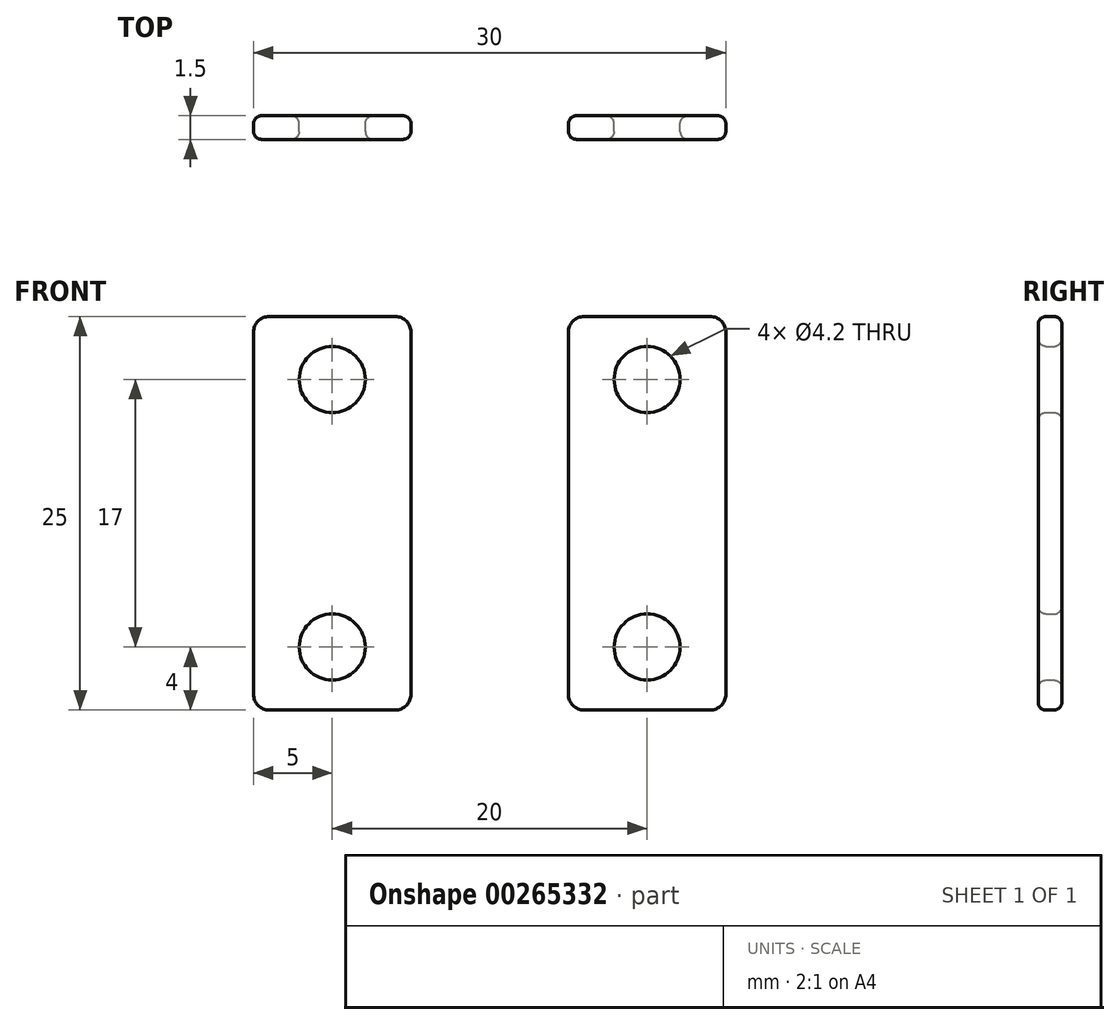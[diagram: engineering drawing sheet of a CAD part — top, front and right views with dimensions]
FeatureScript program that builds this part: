
annotation { "Feature Type Name" : "Feature", "Feature Type Description" : "" }
export const myFeature = defineFeature(function(context is Context, id is Id, definition is map)
    precondition{}
    {
        {
            var Q0;
            Q0=qCreatedBy(makeId("Front.planeOp"),FACE);
            var sketch = newSketch(context, id + "F0", { "sketchPlane" : qUnion([Q0])});
            skLineSegment(sketch, "E0.bottom", {"start": v(6, 12.5) * mm, "end": v(14, 12.5) * mm});
            skLineSegment(sketch, "E0.top", {"start": v(6, -12.5) * mm, "end": v(14, -12.5) * mm});
            skLineSegment(sketch, "E0.left", {"start": v(5, 11.5) * mm, "end": v(5, -11.5) * mm});
            skLineSegment(sketch, "E0.right", {"start": v(15, 11.5) * mm, "end": v(15, -11.5) * mm});
            skCircle(sketch, "E1", {"center": v(10, 8.5) * mm, "radius": 2.1 * mm});
            skCircle(sketch, "E2", {"center": v(10, -8.5) * mm, "radius": 2.1 * mm});
            skPoint(sketch, "E3.visualSharp", {"position": v(5, 12.5) * mm});
            skArc(sketch, "E3.filletArc", {"start": v(6, 12.5) * mm, "mid": v(5.3, 12.2) * mm, "end": v(5, 11.5) * mm});
            skPoint(sketch, "E4.visualSharp", {"position": v(15, 12.5) * mm});
            skArc(sketch, "E4.filletArc", {"start": v(15, 11.5) * mm, "mid": v(14.7, 12.2) * mm, "end": v(14, 12.5) * mm});
            skPoint(sketch, "E5.visualSharp", {"position": v(15, -12.5) * mm});
            skArc(sketch, "E5.filletArc", {"start": v(14, -12.5) * mm, "mid": v(14.7, -12.2) * mm, "end": v(15, -11.5) * mm});
            skPoint(sketch, "E6.visualSharp", {"position": v(5, -12.5) * mm});
            skArc(sketch, "E6.filletArc", {"start": v(5, -11.5) * mm, "mid": v(5.3, -12.2) * mm, "end": v(6, -12.5) * mm});
            skLineSegment(sketch, "E7.MirrorCS", {"start": v(-6, 12.5) * mm, "end": v(-14, 12.5) * mm});
            skLineSegment(sketch, "E8.MirrorCS", {"start": v(-15, 11.5) * mm, "end": v(-15, -11.5) * mm});
            skLineSegment(sketch, "E9.MirrorCS", {"start": v(-6, -12.5) * mm, "end": v(-14, -12.5) * mm});
            skLineSegment(sketch, "E10.MirrorCS", {"start": v(-5, 11.5) * mm, "end": v(-5, -11.5) * mm});
            skCircle(sketch, "E11.MirrorC", {"center": v(-10, 8.5) * mm, "radius": 2.1 * mm});
            skCircle(sketch, "E12.MirrorC", {"center": v(-10, -8.5) * mm, "radius": 2.1 * mm});
            skArc(sketch, "E13.MirrorCS", {"start": v(-5, -11.5) * mm, "mid": v(-5.3, -12.2) * mm, "end": v(-6, -12.5) * mm});
            skArc(sketch, "E14.MirrorCS", {"start": v(-14, -12.5) * mm, "mid": v(-14.7, -12.2) * mm, "end": v(-15, -11.5) * mm});
            skArc(sketch, "E15.MirrorCS", {"start": v(-15, 11.5) * mm, "mid": v(-14.7, 12.2) * mm, "end": v(-14, 12.5) * mm});
            skArc(sketch, "E16.MirrorCS", {"start": v(-6, 12.5) * mm, "mid": v(-5.3, 12.2) * mm, "end": v(-5, 11.5) * mm});
            skSolve(sketch);
        }
        {
            var Q0;
            Q0 = qSketchRegion(id + "F0", true);
            extrude(context, id + "F1", {"entities" : qUnion([Q0]), "depth" : 1.5 * mm});
        }
        {
            var Q0;
            Q0=makeQuery(id+"F1.opExtrude","CAP_EDGE",EDGE,{"disambiguationData":[OSD([sQuery(id+"F0.wireOp",EDGE,"E8.MirrorCS")])],"isStart":false});
            var Q1;
            Q1=makeQuery(id+"F1.opExtrude","CAP_EDGE",EDGE,{"disambiguationData":[OSD([sQuery(id+"F0.wireOp",EDGE,"E0.left")])],"isStart":false});
            var Q2;
            Q2=makeQuery(id+"F1.opExtrude","CAP_EDGE",EDGE,{"disambiguationData":[OSD([sQuery(id+"F0.wireOp",EDGE,"E11.MirrorC")])],"isStart":false});
            var Q3;
            Q3=makeQuery(id+"F1.opExtrude","CAP_EDGE",EDGE,{"disambiguationData":[OSD([sQuery(id+"F0.wireOp",EDGE,"E12.MirrorC")])],"isStart":false});
            var Q4;
            Q4=makeQuery(id+"F1.opExtrude","CAP_EDGE",EDGE,{"disambiguationData":[OSD([sQuery(id+"F0.wireOp",EDGE,"E1")])],"isStart":false});
            var Q5;
            Q5=makeQuery(id+"F1.opExtrude","CAP_EDGE",EDGE,{"disambiguationData":[OSD([sQuery(id+"F0.wireOp",EDGE,"E2")])],"isStart":false});
            var Q6;
            Q6=makeQuery(id+"F1.opExtrude","CAP_EDGE",EDGE,{"disambiguationData":[OSD([sQuery(id+"F0.wireOp",EDGE,"E8.MirrorCS")])],"isStart":true});
            var Q7;
            Q7=makeQuery(id+"F1.opExtrude","CAP_EDGE",EDGE,{"disambiguationData":[OSD([sQuery(id+"F0.wireOp",EDGE,"E12.MirrorC")])],"isStart":true});
            var Q8;
            Q8=makeQuery(id+"F1.opExtrude","CAP_EDGE",EDGE,{"disambiguationData":[OSD([sQuery(id+"F0.wireOp",EDGE,"E11.MirrorC")])],"isStart":true});
            var Q9;
            Q9=makeQuery(id+"F1.opExtrude","CAP_EDGE",EDGE,{"disambiguationData":[OSD([sQuery(id+"F0.wireOp",EDGE,"E0.left")])],"isStart":true});
            var Q10;
            Q10=makeQuery(id+"F1.opExtrude","CAP_EDGE",EDGE,{"disambiguationData":[OSD([sQuery(id+"F0.wireOp",EDGE,"E2")])],"isStart":true});
            var Q11;
            Q11=makeQuery(id+"F1.opExtrude","CAP_EDGE",EDGE,{"disambiguationData":[OSD([sQuery(id+"F0.wireOp",EDGE,"E1")])],"isStart":true});
            fillet(context, id + "F2", {"entities" : qUnion([Q0, Q1, Q2, Q3, Q4, Q5, Q6, Q7, Q8, Q9, Q10, Q11]), "radius" : .5 * mm, "tangentPropagation" : true, "allowEdgeOverflow" : false});
        }
    });
